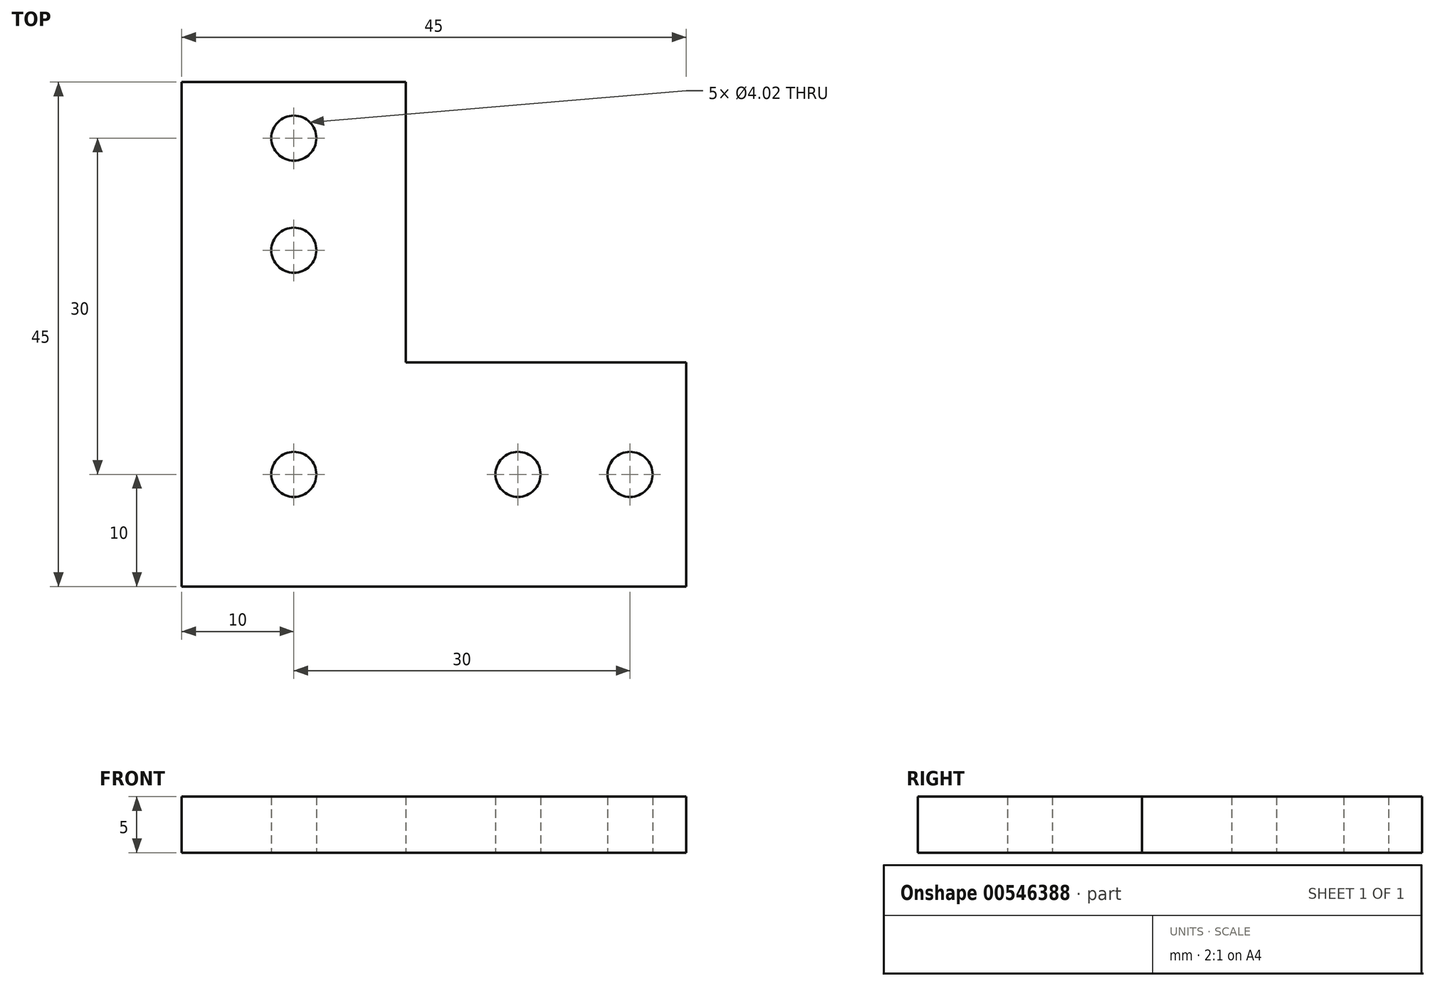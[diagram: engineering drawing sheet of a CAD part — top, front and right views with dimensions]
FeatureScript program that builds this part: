
annotation { "Feature Type Name" : "Feature", "Feature Type Description" : "" }
export const myFeature = defineFeature(function(context is Context, id is Id, definition is map)
    precondition{}
    {
        {
            var Q0;
            Q0=qCreatedBy(makeId("Top.planeOp"),FACE);
            var sketch = newSketch(context, id + "F0", { "sketchPlane" : qUnion([Q0])});
            skLineSegment(sketch, "E0", {"start": v(0, 0) * mm, "end": v(0, 45) * mm});
            skLineSegment(sketch, "E1", {"start": v(0, 45) * mm, "end": v(20, 45) * mm});
            skLineSegment(sketch, "E2", {"start": v(20, 45) * mm, "end": v(20, 20) * mm});
            skLineSegment(sketch, "E3", {"start": v(20, 20) * mm, "end": v(45, 20) * mm});
            skLineSegment(sketch, "E4", {"start": v(45, 20) * mm, "end": v(45, 0) * mm});
            skLineSegment(sketch, "E5", {"start": v(45, 0) * mm, "end": v(0, 0) * mm});
            skCircle(sketch, "E6", {"center": v(10, 10) * mm, "radius": 2 * mm});
            skCircle(sketch, "E7", {"center": v(30, 10) * mm, "radius": 2 * mm});
            skCircle(sketch, "E8", {"center": v(40, 10) * mm, "radius": 2 * mm});
            skCircle(sketch, "E9", {"center": v(10, 40) * mm, "radius": 2 * mm});
            skCircle(sketch, "E10", {"center": v(10, 30) * mm, "radius": 2 * mm});
            skSolve(sketch);
        }
        {
            var Q0;
            Q0=qSketchRegion(id+"F0",true);
            extrude(context, id + "F1", {"entities" : qUnion([Q0]), "depth" : 5 * mm});
        }
    });
